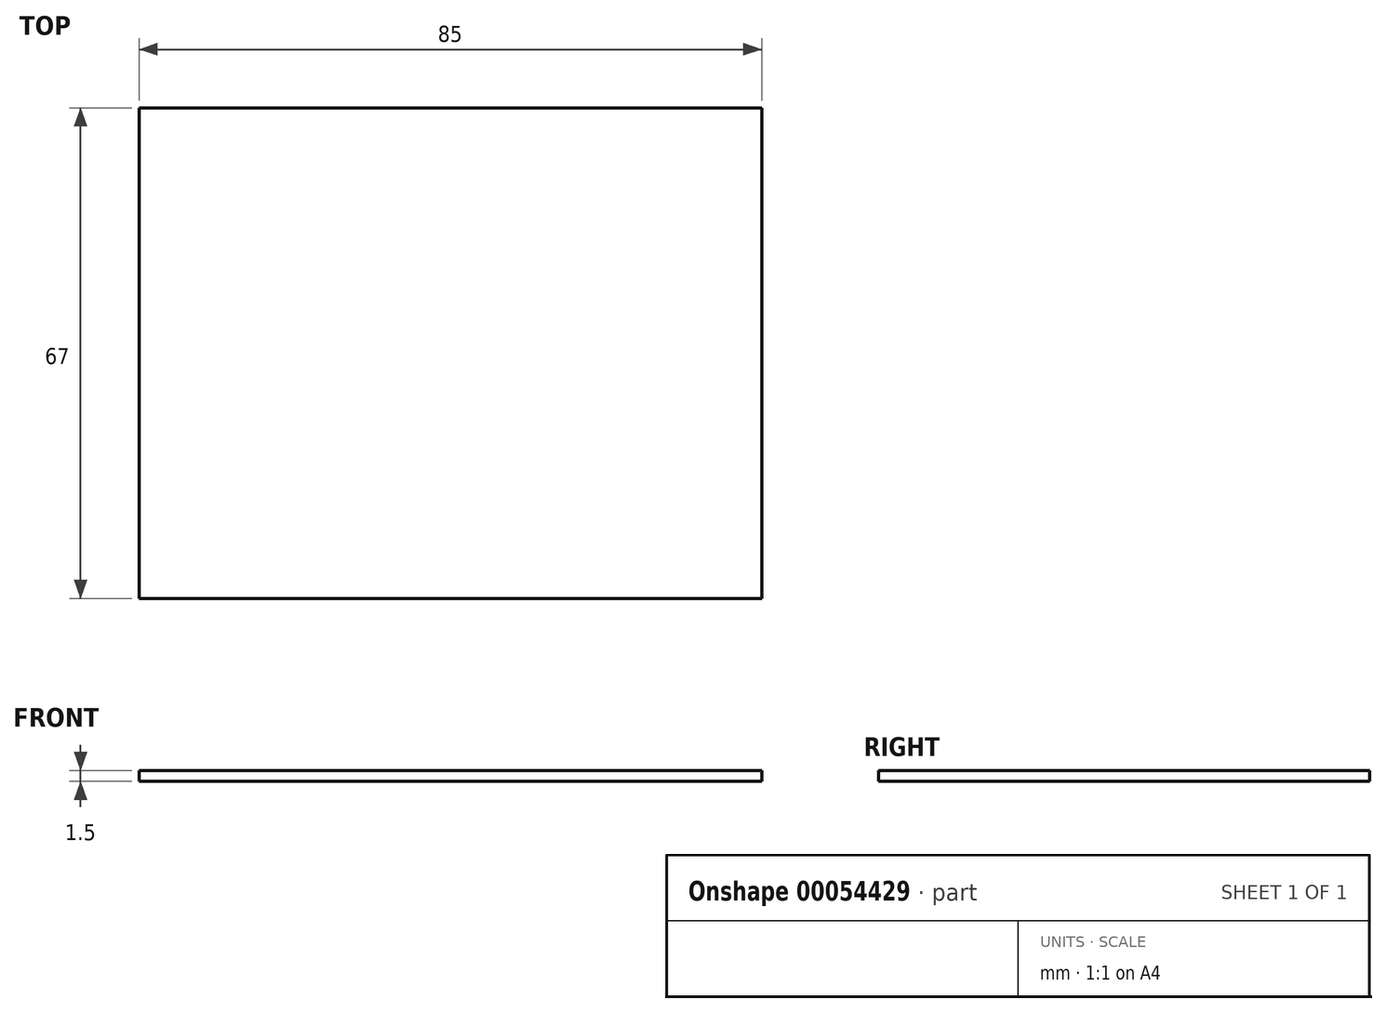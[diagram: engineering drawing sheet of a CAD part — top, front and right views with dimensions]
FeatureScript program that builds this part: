
annotation { "Feature Type Name" : "Feature", "Feature Type Description" : "" }
export const myFeature = defineFeature(function(context is Context, id is Id, definition is map)
    precondition{}
    {
        {
            var Q0;
            Q0=qCreatedBy(makeId("Top.planeOp"),FACE);
            var sketch = newSketch(context, id + "F0", { "sketchPlane" : qUnion([Q0])});
            skLineSegment(sketch, "E0.bottom", {"start": v(-43.8, 8.05) * mm, "end": v(41.2, 8.05) * mm});
            skLineSegment(sketch, "E0.top", {"start": v(-43.8, -58.95) * mm, "end": v(41.2, -58.95) * mm});
            skLineSegment(sketch, "E0.left", {"start": v(-43.8, 8.05) * mm, "end": v(-43.8, -58.95) * mm});
            skLineSegment(sketch, "E0.right", {"start": v(41.2, 8.05) * mm, "end": v(41.2, -58.95) * mm});
            skSolve(sketch);
        }
        {
            var Q0;
            Q0=makeQuery(id+"F0.imprint","IMPRINT",FACE,{"disambiguationData":[TD([[makeQuery(id+"F0.imprint","IMPRINT",EDGE,{"derivedFrom":sQuery(id+"F0.wireOp",EDGE,"E0.bottom")}),-1.0]])]});
            extrude(context, id + "F1", {"entities" : qUnion([Q0]), "depth" : 1.5 * mm});
        }
    });
